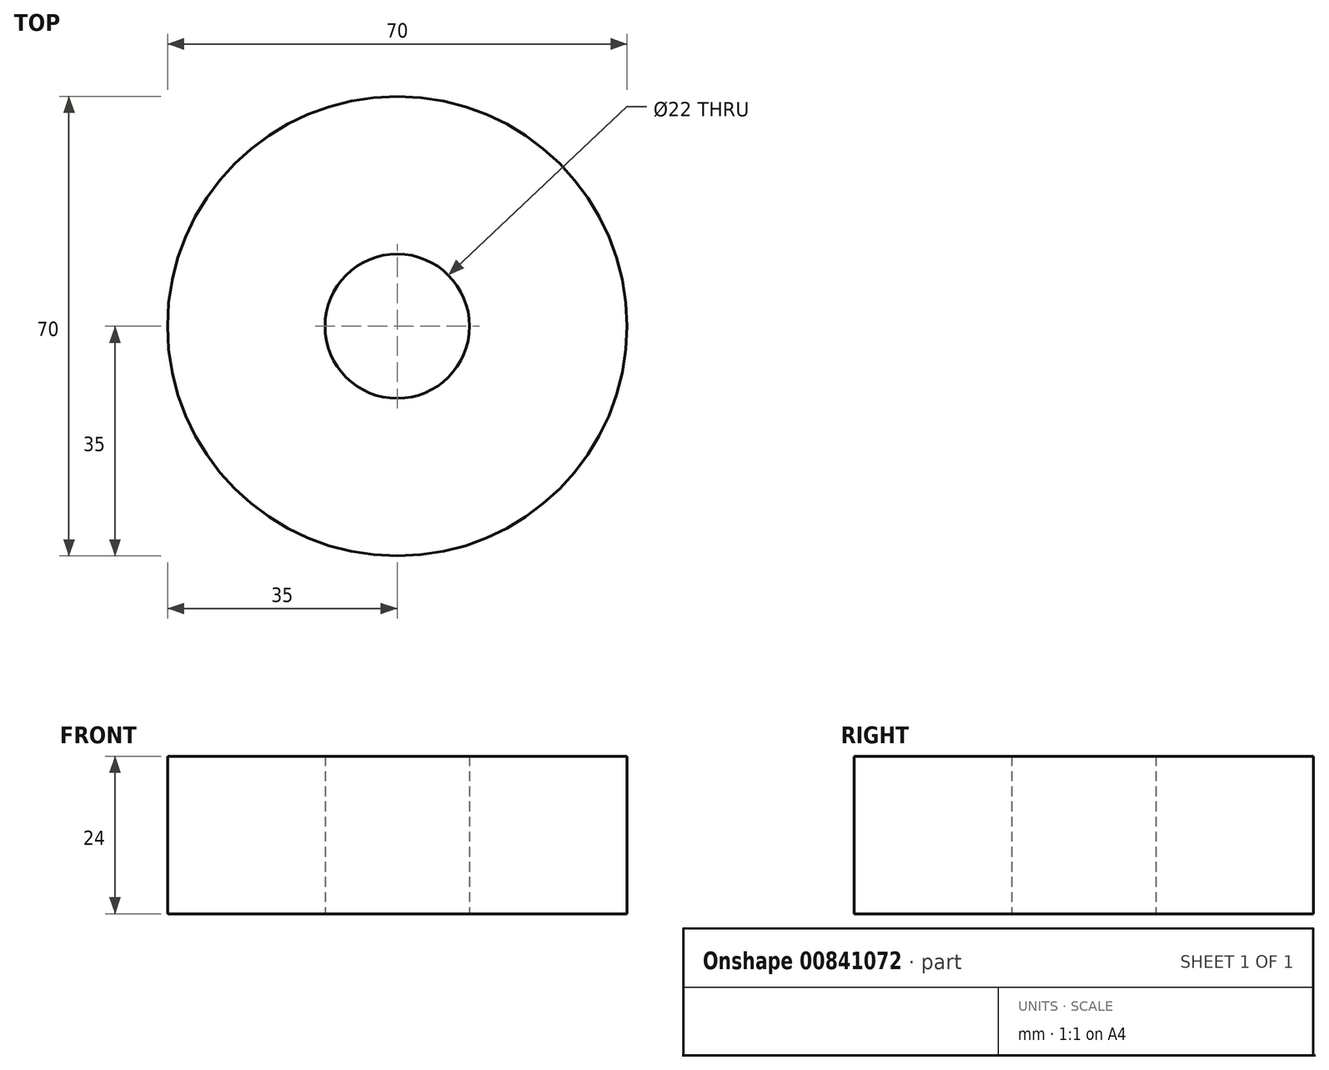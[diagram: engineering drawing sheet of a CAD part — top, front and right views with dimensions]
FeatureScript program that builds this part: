
annotation { "Feature Type Name" : "Feature", "Feature Type Description" : "" }
export const myFeature = defineFeature(function(context is Context, id is Id, definition is map)
    precondition{}
    {
        {
            var Q0;
            Q0=qCreatedBy(makeId("Top.planeOp"),FACE);
            var sketch = newSketch(context, id + "F0", { "sketchPlane" : qUnion([Q0])});
            skCircle(sketch, "E0", {"center": v(0, 0) * mm, "radius": 35 * mm});
            skCircle(sketch, "E1", {"center": v(0, 0) * mm, "radius": 11 * mm});
            skSolve(sketch);
        }
        {
            var Q0;
            Q0=makeQuery(id+"F0.imprint","IMPRINT",FACE,{"disambiguationData":[TD([[makeQuery(id+"F0.imprint","IMPRINT",EDGE,{"derivedFrom":sQuery(id+"F0.wireOp",EDGE,"E0")}),1.0]])]});
            extrude(context, id + "F1", {"entities" : qUnion([Q0]), "depth" : 24 * mm, "offsetDistance" : 25 * mm});
        }
    });
